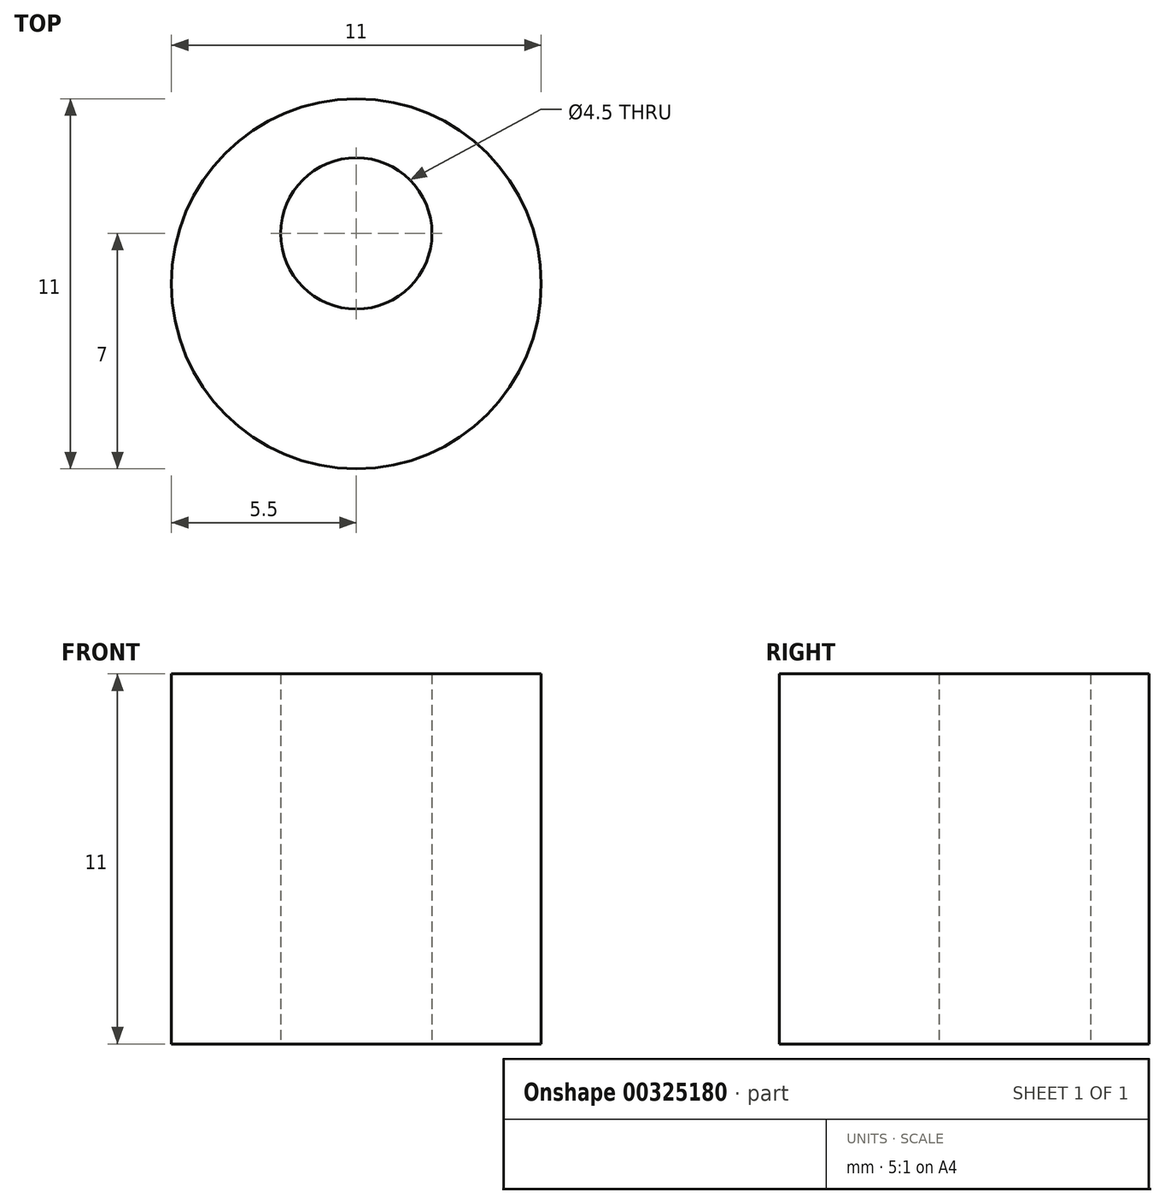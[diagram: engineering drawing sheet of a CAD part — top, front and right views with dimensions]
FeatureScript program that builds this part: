
annotation { "Feature Type Name" : "Feature", "Feature Type Description" : "" }
export const myFeature = defineFeature(function(context is Context, id is Id, definition is map)
    precondition{}
    {
        {
            var Q0;
            Q0=qCreatedBy(makeId("Top.planeOp"),FACE);
            var sketch = newSketch(context, id + "F0", { "sketchPlane" : qUnion([Q0])});
            skCircle(sketch, "E0", {"center": v(0, 0) * mm, "radius": 5.5 * mm});
            skCircle(sketch, "E1", {"center": v(0, 1.5) * mm, "radius": 2.25 * mm});
            skSolve(sketch);
        }
        {
            var Q0;
            Q0 = qSketchRegion(id + "F0", true);
            extrude(context, id + "F1", {"entities" : qUnion([Q0]), "depth" : 11 * mm});
        }
    });
